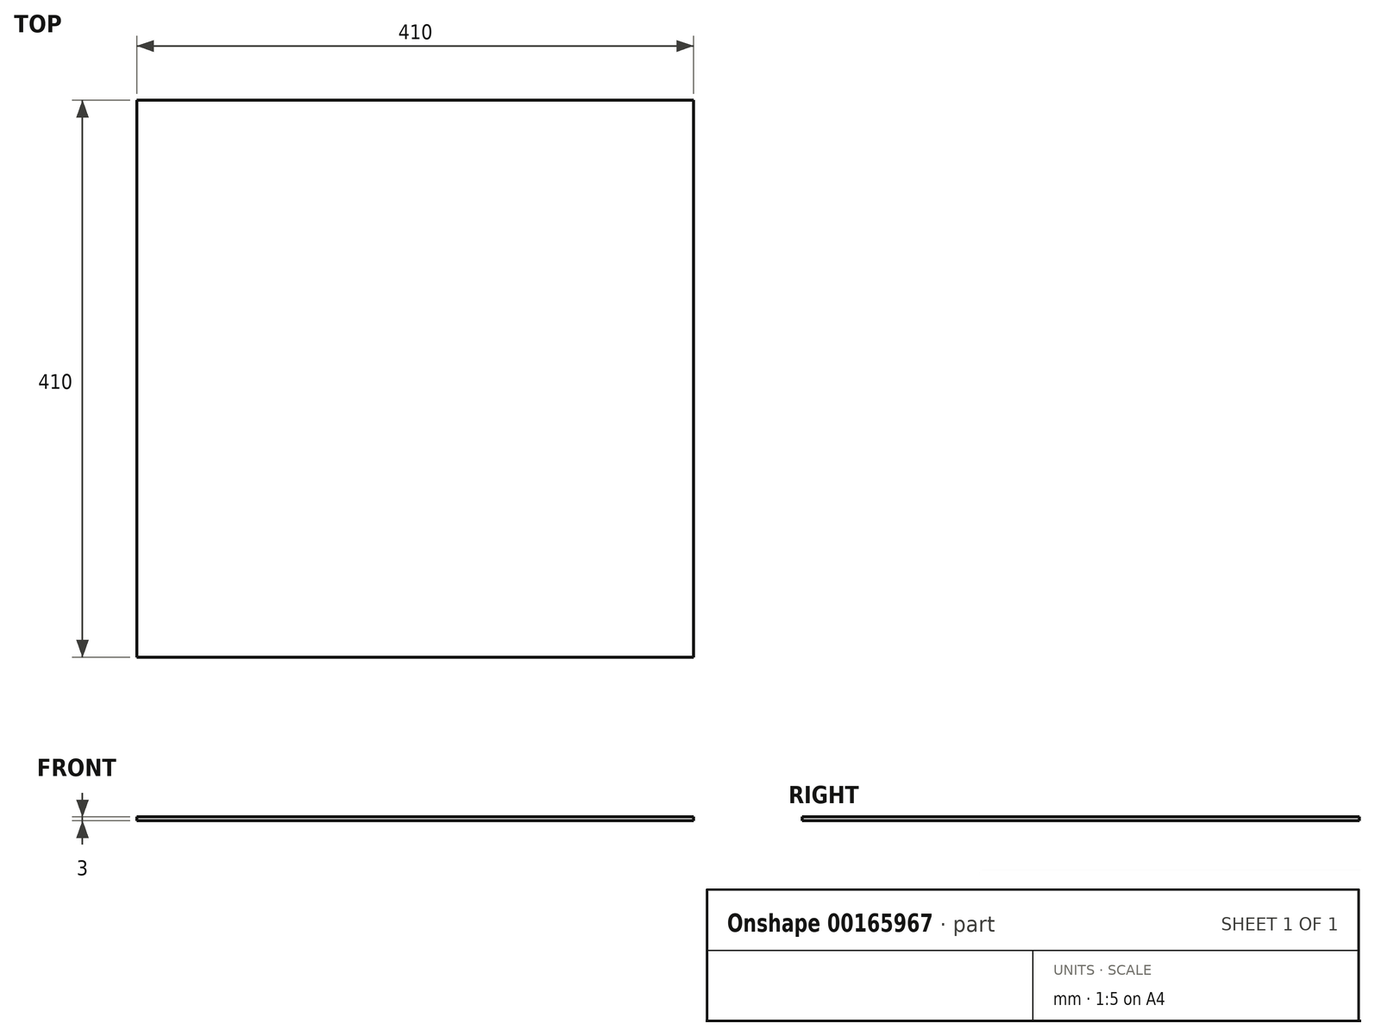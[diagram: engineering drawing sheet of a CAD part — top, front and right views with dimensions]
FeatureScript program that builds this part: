
annotation { "Feature Type Name" : "Feature", "Feature Type Description" : "" }
export const myFeature = defineFeature(function(context is Context, id is Id, definition is map)
    precondition{}
    {
        {
            var Q0;
            Q0=qCreatedBy(makeId("Top.planeOp"),FACE);
            var sketch = newSketch(context, id + "F0", { "sketchPlane" : qUnion([Q0])});
            skLineSegment(sketch, "E0.bottom", {"start": v(205, -205) * mm, "end": v(-205, -205) * mm});
            skLineSegment(sketch, "E0.top", {"start": v(205, 205) * mm, "end": v(-205, 205) * mm});
            skLineSegment(sketch, "E0.left", {"start": v(205, -205) * mm, "end": v(205, 205) * mm});
            skLineSegment(sketch, "E0.right", {"start": v(-205, -205) * mm, "end": v(-205, 205) * mm});
            skPoint(sketch, "E0.middle", {"position": v(0, 0) * mm});
            skSolve(sketch);
        }
        {
            var Q0;
            Q0 = qSketchRegion(id + "F0", true);
            extrude(context, id + "F1", {"entities" : qUnion([Q0]), "depth" : 3 * mm});
        }
    });
